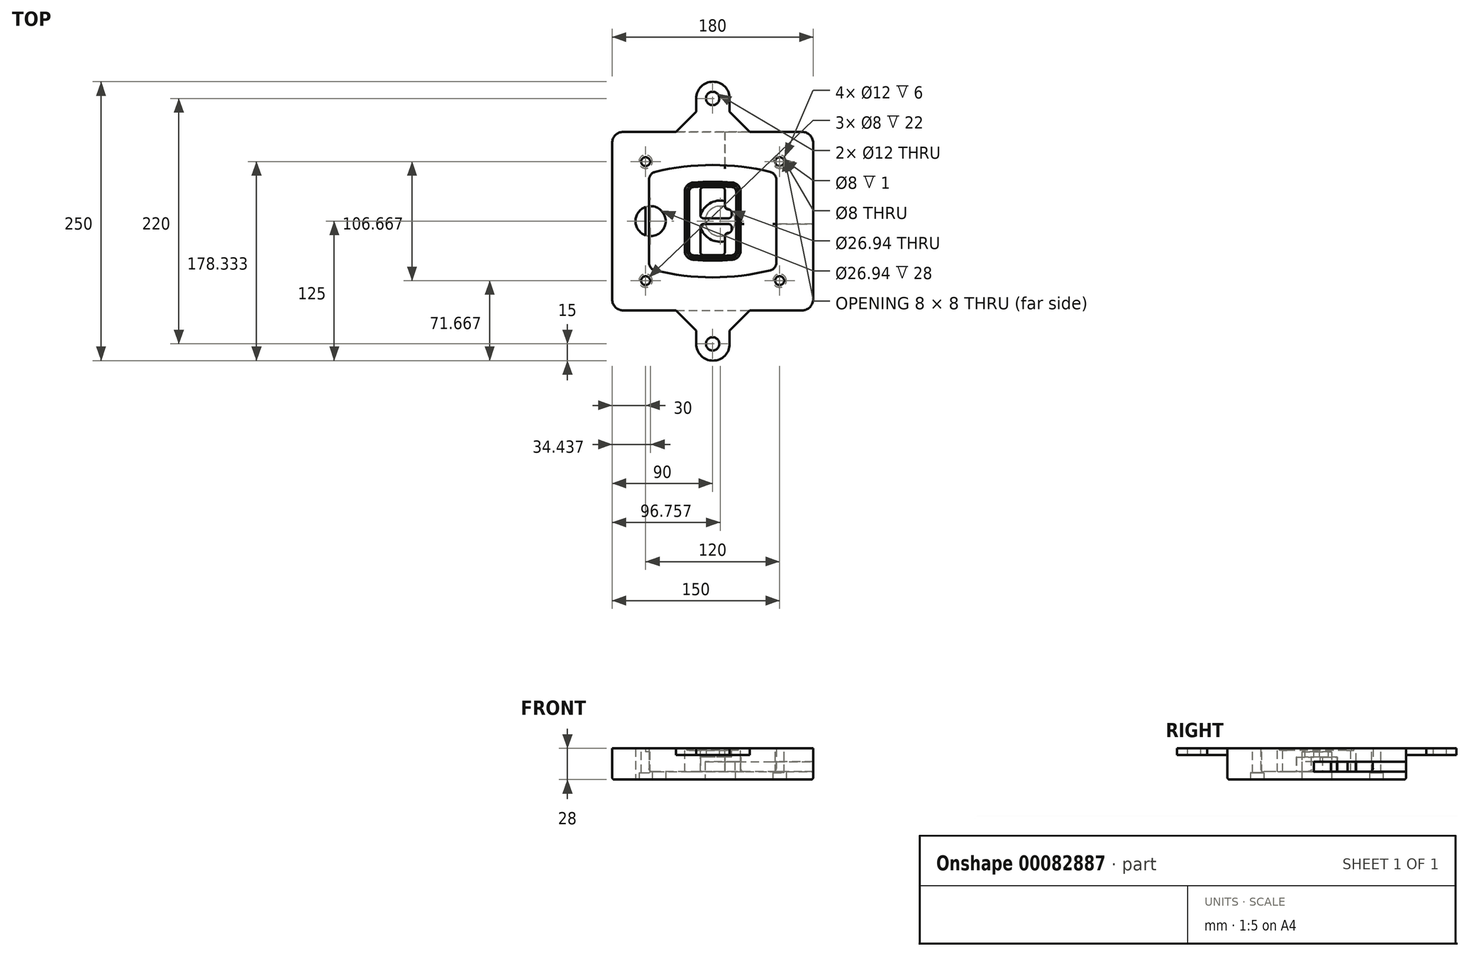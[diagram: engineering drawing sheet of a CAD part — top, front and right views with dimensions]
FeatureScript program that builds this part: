
annotation { "Feature Type Name" : "Feature", "Feature Type Description" : "" }
export const myFeature = defineFeature(function(context is Context, id is Id, definition is map)
    precondition{}
    {
        {
            var Q0;
            Q0=qCreatedBy(makeId("Top.planeOp"),FACE);
            var sketch = newSketch(context, id + "F0", { "sketchPlane" : qUnion([Q0])});
            skPoint(sketch, "E0.rect.middle", {"position": v(0, 0) * mm});
            skLineSegment(sketch, "E1.bottom", {"start": v(-80, -80) * mm, "end": v(80, -80) * mm});
            skLineSegment(sketch, "E1.top", {"start": v(-80, 80) * mm, "end": v(80, 80) * mm});
            skLineSegment(sketch, "E1.left", {"start": v(-90, -70) * mm, "end": v(-90, 70) * mm});
            skLineSegment(sketch, "E1.right", {"start": v(90, -70) * mm, "end": v(90, 70) * mm});
            skLineSegment(sketch, "E2", {"start": v(-90, 80) * mm, "end": v(90, -80) * mm, "construction": true});
            skLineSegment(sketch, "E3", {"start": v(90, 80) * mm, "end": v(-90, -80) * mm, "construction": true});
            skCircle(sketch, "E4", {"center": v(-60, 53.33) * mm, "radius": 4 * mm});
            skCircle(sketch, "E5", {"center": v(60, 53.33) * mm, "radius": 4 * mm});
            skCircle(sketch, "E6", {"center": v(60, -53.33) * mm, "radius": 4 * mm});
            skCircle(sketch, "E7", {"center": v(-60, -53.33) * mm, "radius": 4 * mm});
            skLineSegment(sketch, "E8", {"start": v(-60, 53.33) * mm, "end": v(60, 53.33) * mm, "construction": true});
            skLineSegment(sketch, "E9", {"start": v(60, 53.33) * mm, "end": v(60, -53.33) * mm, "construction": true});
            skLineSegment(sketch, "E10", {"start": v(60, -53.33) * mm, "end": v(-60, -53.33) * mm, "construction": true});
            skLineSegment(sketch, "E11", {"start": v(-60, -53.33) * mm, "end": v(-60, 53.33) * mm, "construction": true});
            skLineSegment(sketch, "E12", {"start": v(-60, 37.3) * mm, "end": v(-60, -37.3) * mm});
            skLineSegment(sketch, "E13", {"start": v(60, 37.3) * mm, "end": v(60, -37.3) * mm});
            skArc(sketch, "E14", {"start": v(52.38, 47.01) * mm, "mid": v(0, 53.33) * mm, "end": v(-52.38, 47.01) * mm});
            skArc(sketch, "E15", {"start": v(-52.38, -47.01) * mm, "mid": v(0, -53.33) * mm, "end": v(52.38, -47.01) * mm});
            skLineSegment(sketch, "E16", {"start": v(-60, 0) * mm, "end": v(60, 0) * mm, "construction": true});
            skPoint(sketch, "E17.visualSharp", {"position": v(-60, -45) * mm});
            skArc(sketch, "E17.filletArc", {"start": v(-60, -37.3) * mm, "mid": v(-57.87, -43.47) * mm, "end": v(-52.38, -47.01) * mm});
            skPoint(sketch, "E18.visualSharp", {"position": v(-60, 45) * mm});
            skArc(sketch, "E18.filletArc", {"start": v(-52.38, 47.01) * mm, "mid": v(-57.87, 43.47) * mm, "end": v(-60, 37.3) * mm});
            skPoint(sketch, "E19.visualSharp", {"position": v(60, 45) * mm});
            skArc(sketch, "E19.filletArc", {"start": v(60, 37.3) * mm, "mid": v(57.87, 43.47) * mm, "end": v(52.38, 47.01) * mm});
            skPoint(sketch, "E20.visualSharp", {"position": v(60, -45) * mm});
            skArc(sketch, "E20.filletArc", {"start": v(52.38, -47.01) * mm, "mid": v(57.87, -43.47) * mm, "end": v(60, -37.3) * mm});
            skPoint(sketch, "E21.visualSharp", {"position": v(-90, 80) * mm});
            skArc(sketch, "E21.filletArc", {"start": v(-80, 80) * mm, "mid": v(-87.07, 77.07) * mm, "end": v(-90, 70) * mm});
            skPoint(sketch, "E22.visualSharp", {"position": v(90, 80) * mm});
            skArc(sketch, "E22.filletArc", {"start": v(90, 70) * mm, "mid": v(87.07, 77.07) * mm, "end": v(80, 80) * mm});
            skPoint(sketch, "E23.visualSharp", {"position": v(90, -80) * mm});
            skArc(sketch, "E23.filletArc", {"start": v(80, -80) * mm, "mid": v(87.07, -77.07) * mm, "end": v(90, -70) * mm});
            skPoint(sketch, "E24.visualSharp", {"position": v(-90, -80) * mm});
            skArc(sketch, "E24.filletArc", {"start": v(-90, -70) * mm, "mid": v(-87.07, -77.07) * mm, "end": v(-80, -80) * mm});
            skArc(sketch, "E25.0", {"start": v(57, 37.3) * mm, "mid": v(55.5, 41.62) * mm, "end": v(51.67, 44.1) * mm});
            skLineSegment(sketch, "E25.1", {"start": v(57, 37.3) * mm, "end": v(57, -37.3) * mm});
            skArc(sketch, "E25.2", {"start": v(51.67, -44.1) * mm, "mid": v(55.5, -41.62) * mm, "end": v(57, -37.3) * mm});
            skArc(sketch, "E25.3", {"start": v(-51.67, -44.1) * mm, "mid": v(0, -50.33) * mm, "end": v(51.67, -44.1) * mm});
            skArc(sketch, "E25.4", {"start": v(-57, -37.3) * mm, "mid": v(-55.5, -41.62) * mm, "end": v(-51.67, -44.1) * mm});
            skArc(sketch, "E25.5", {"start": v(51.67, 44.1) * mm, "mid": v(0, 50.33) * mm, "end": v(-51.67, 44.1) * mm});
            skLineSegment(sketch, "E25.6", {"start": v(-57, 37.3) * mm, "end": v(-57, -37.3) * mm});
            skArc(sketch, "E25.7", {"start": v(-51.67, 44.1) * mm, "mid": v(-55.5, 41.62) * mm, "end": v(-57, 37.3) * mm});
            skArc(sketch, "E26.0", {"start": v(-53.33, 50.9) * mm, "mid": v(-61.01, 45.94) * mm, "end": v(-64, 37.3) * mm});
            skArc(sketch, "E26.1", {"start": v(53.33, 50.9) * mm, "mid": v(0, 57.33) * mm, "end": v(-53.33, 50.9) * mm});
            skArc(sketch, "E26.2", {"start": v(64, 37.3) * mm, "mid": v(61.01, 45.94) * mm, "end": v(53.33, 50.9) * mm});
            skLineSegment(sketch, "E26.3", {"start": v(64, 37.3) * mm, "end": v(64, -37.3) * mm});
            skArc(sketch, "E26.4", {"start": v(53.33, -50.9) * mm, "mid": v(61.01, -45.94) * mm, "end": v(64, -37.3) * mm});
            skLineSegment(sketch, "E26.5", {"start": v(-64, 37.3) * mm, "end": v(-64, -37.3) * mm});
            skArc(sketch, "E26.6", {"start": v(-53.33, -50.9) * mm, "mid": v(0, -57.33) * mm, "end": v(53.33, -50.9) * mm});
            skArc(sketch, "E26.7", {"start": v(-64, -37.3) * mm, "mid": v(-61.01, -45.94) * mm, "end": v(-53.33, -50.9) * mm});
            skSolve(sketch);
        }
        {
            var Q0;
            Q0=makeQuery(id+"F0.imprint","IMPRINT",FACE,{"disambiguationData":[TD([[makeQuery(id+"F0.imprint","IMPRINT",EDGE,{"derivedFrom":sQuery(id+"F0.wireOp",EDGE,"E1.bottom")}),1.0]])]});
            var Q1;
            Q1=makeQuery(id+"F0.imprint","IMPRINT",FACE,{"disambiguationData":[TD([[makeQuery(id+"F0.imprint","IMPRINT",EDGE,{"derivedFrom":sQuery(id+"F0.wireOp",EDGE,"E12")}),1.0]])]});
            var Q2;
            Q2=makeQuery(id+"F0.imprint","IMPRINT",FACE,{"disambiguationData":[TD([[makeQuery(id+"F0.imprint","IMPRINT",EDGE,{"derivedFrom":sQuery(id+"F0.wireOp",EDGE,"E25.0")}),1.0]])]});
            var Q3;
            Q3=makeQuery(id+"F0.imprint","IMPRINT",FACE,{"disambiguationData":[TD([[makeQuery(id+"F0.imprint","IMPRINT",EDGE,{"derivedFrom":sQuery(id+"F0.wireOp",EDGE,"E12")}),-1.0]])]});
            extrude(context, id + "F1", {"entities" : qUnion([Q0, Q1, Q2, Q3]), "oppositeDirection" : true, "depth" : 25 * mm});
        }
        {
            var Q0;
            Q0=makeQuery(id+"F0.imprint","IMPRINT",FACE,{"disambiguationData":[TD([[makeQuery(id+"F0.imprint","IMPRINT",EDGE,{"derivedFrom":sQuery(id+"F0.wireOp",EDGE,"E12")}),1.0]])]});
            extrude(context, id + "F2", {"entities" : qUnion([Q0]), "operationType" : NewBodyOperationType.ADD, "depth" : 3 * mm});
        }
        {
            var Q0;
            Q0=makeQuery(id+"F0.imprint","IMPRINT",FACE,{"disambiguationData":[TD([[makeQuery(id+"F0.imprint","IMPRINT",EDGE,{"derivedFrom":sQuery(id+"F0.wireOp",EDGE,"E25.0")}),1.0]])]});
            extrude(context, id + "F3", {"entities" : qUnion([Q0]), "operationType" : NewBodyOperationType.REMOVE, "oppositeDirection" : true, "depth" : 18 * mm});
        }
        {
            var Q0;
            Q0=makeQuery(id+"F2.opExtrude","CAP_FACE",FACE,{"disambiguationData":[OSD([sQuery(id+"F0.wireOp",EDGE,"E12"),sQuery(id+"F0.wireOp",EDGE,"E13"),sQuery(id+"F0.wireOp",EDGE,"E14"),sQuery(id+"F0.wireOp",EDGE,"E15"),sQuery(id+"F0.wireOp",EDGE,"E17.filletArc"),sQuery(id+"F0.wireOp",EDGE,"E18.filletArc"),sQuery(id+"F0.wireOp",EDGE,"E19.filletArc"),sQuery(id+"F0.wireOp",EDGE,"E20.filletArc"),sQuery(id+"F0.wireOp",EDGE,"E25.0"),sQuery(id+"F0.wireOp",EDGE,"E25.1"),sQuery(id+"F0.wireOp",EDGE,"E25.2"),sQuery(id+"F0.wireOp",EDGE,"E25.3"),sQuery(id+"F0.wireOp",EDGE,"E25.4"),sQuery(id+"F0.wireOp",EDGE,"E25.5"),sQuery(id+"F0.wireOp",EDGE,"E25.6"),sQuery(id+"F0.wireOp",EDGE,"E25.7")])],"isStart":false});
            var sketch = newSketch(context, id + "F4", { "sketchPlane" : qUnion([Q0])});
            skArc(sketch, "E27.0", {"start": v(-17.7, -34.56) * mm, "mid": v(0, -35.33) * mm, "end": v(17.7, -34.56) * mm});
            skArc(sketch, "E28.0", {"start": v(17.7, 34.56) * mm, "mid": v(0, 35.33) * mm, "end": v(-17.7, 34.56) * mm});
            skLineSegment(sketch, "E29", {"start": v(-25, 26.59) * mm, "end": v(-25, -26.59) * mm});
            skLineSegment(sketch, "E30", {"start": v(25, 26.59) * mm, "end": v(25, -26.59) * mm});
            skLineSegment(sketch, "E31", {"start": v(-25, 33.78) * mm, "end": v(25, 33.78) * mm, "construction": true});
            skLineSegment(sketch, "E32", {"start": v(-25, -33.78) * mm, "end": v(25, -33.78) * mm, "construction": true});
            skPoint(sketch, "E33.visualSharp", {"position": v(-25, 33.78) * mm});
            skArc(sketch, "E33.filletArc", {"start": v(-17.7, 34.56) * mm, "mid": v(-22.9, 32) * mm, "end": v(-25, 26.59) * mm});
            skPoint(sketch, "E34.visualSharp", {"position": v(25, 33.78) * mm});
            skArc(sketch, "E34.filletArc", {"start": v(25, 26.59) * mm, "mid": v(22.9, 32) * mm, "end": v(17.7, 34.56) * mm});
            skPoint(sketch, "E35.visualSharp", {"position": v(25, -33.78) * mm});
            skArc(sketch, "E35.filletArc", {"start": v(17.7, -34.56) * mm, "mid": v(22.9, -32) * mm, "end": v(25, -26.59) * mm});
            skPoint(sketch, "E36.visualSharp", {"position": v(-25, -33.78) * mm});
            skArc(sketch, "E36.filletArc", {"start": v(-25, -26.59) * mm, "mid": v(-22.9, -32) * mm, "end": v(-17.7, -34.56) * mm});
            skArc(sketch, "E37.0", {"start": v(51.67, 44.1) * mm, "mid": v(0, 50.33) * mm, "end": v(-51.67, 44.1) * mm});
            skArc(sketch, "E37.1", {"start": v(-51.67, 44.1) * mm, "mid": v(-55.5, 41.62) * mm, "end": v(-57, 37.3) * mm});
            skLineSegment(sketch, "E37.2", {"start": v(-57, 37.3) * mm, "end": v(-57, -37.3) * mm});
            skArc(sketch, "E37.3", {"start": v(-57, -37.3) * mm, "mid": v(-55.5, -41.62) * mm, "end": v(-51.67, -44.1) * mm});
            skArc(sketch, "E37.4", {"start": v(-51.67, -44.1) * mm, "mid": v(0, -50.33) * mm, "end": v(51.67, -44.1) * mm});
            skArc(sketch, "E37.5", {"start": v(51.67, -44.1) * mm, "mid": v(55.5, -41.62) * mm, "end": v(57, -37.3) * mm});
            skLineSegment(sketch, "E37.6", {"start": v(57, 37.3) * mm, "end": v(57, -37.3) * mm});
            skArc(sketch, "E37.7", {"start": v(57, 37.3) * mm, "mid": v(55.5, 41.62) * mm, "end": v(51.67, 44.1) * mm});
            skLineSegment(sketch, "E38.0", {"start": v(23, 26.59) * mm, "end": v(23, -26.59) * mm});
            skArc(sketch, "E38.1", {"start": v(17.53, -32.56) * mm, "mid": v(21.42, -30.64) * mm, "end": v(23, -26.59) * mm});
            skArc(sketch, "E38.2", {"start": v(-17.53, -32.56) * mm, "mid": v(0, -33.33) * mm, "end": v(17.53, -32.56) * mm});
            skArc(sketch, "E38.3", {"start": v(-23, -26.59) * mm, "mid": v(-21.42, -30.64) * mm, "end": v(-17.53, -32.56) * mm});
            skLineSegment(sketch, "E38.4", {"start": v(-23, 26.59) * mm, "end": v(-23, -26.59) * mm});
            skArc(sketch, "E38.5", {"start": v(23, 26.59) * mm, "mid": v(21.42, 30.64) * mm, "end": v(17.53, 32.56) * mm});
            skArc(sketch, "E38.6", {"start": v(-17.53, 32.56) * mm, "mid": v(-21.42, 30.64) * mm, "end": v(-23, 26.59) * mm});
            skArc(sketch, "E38.7", {"start": v(17.53, 32.56) * mm, "mid": v(0, 33.33) * mm, "end": v(-17.53, 32.56) * mm});
            skArc(sketch, "E39.0", {"start": v(21, 26.59) * mm, "mid": v(19.95, 29.29) * mm, "end": v(17.35, 30.57) * mm});
            skLineSegment(sketch, "E39.1", {"start": v(21, 26.59) * mm, "end": v(21, -26.59) * mm});
            skArc(sketch, "E39.2", {"start": v(17.35, -30.57) * mm, "mid": v(19.95, -29.29) * mm, "end": v(21, -26.59) * mm});
            skArc(sketch, "E39.3", {"start": v(-17.35, -30.57) * mm, "mid": v(0, -31.33) * mm, "end": v(17.35, -30.57) * mm});
            skArc(sketch, "E39.4", {"start": v(-21, -26.59) * mm, "mid": v(-19.95, -29.29) * mm, "end": v(-17.35, -30.57) * mm});
            skArc(sketch, "E39.5", {"start": v(17.35, 30.57) * mm, "mid": v(0, 31.33) * mm, "end": v(-17.35, 30.57) * mm});
            skLineSegment(sketch, "E39.6", {"start": v(-21, 26.59) * mm, "end": v(-21, -26.59) * mm});
            skArc(sketch, "E39.7", {"start": v(-17.35, 30.57) * mm, "mid": v(-19.95, 29.29) * mm, "end": v(-21, 26.59) * mm});
            skLineSegment(sketch, "E40", {"start": v(-25, 0) * mm, "end": v(25, 0) * mm, "construction": true});
            skLineSegment(sketch, "E41", {"start": v(-11, 5.5) * mm, "end": v(-11, 27.5) * mm});
            skLineSegment(sketch, "E42", {"start": v(-8, 30.5) * mm, "end": v(8, 30.5) * mm});
            skLineSegment(sketch, "E43", {"start": v(11, 27.5) * mm, "end": v(11, 13.5) * mm});
            skLineSegment(sketch, "E44", {"start": v(14, 10.5) * mm, "end": v(14, 10.5) * mm});
            skLineSegment(sketch, "E45", {"start": v(17, 7.5) * mm, "end": v(17, 5.5) * mm});
            skLineSegment(sketch, "E46", {"start": v(14, 2.5) * mm, "end": v(-8, 2.5) * mm});
            skPoint(sketch, "E47.visualSharp", {"position": v(-11, 30.5) * mm});
            skArc(sketch, "E47.filletArc", {"start": v(-8, 30.5) * mm, "mid": v(-10.12, 29.62) * mm, "end": v(-11, 27.5) * mm});
            skPoint(sketch, "E48.visualSharp", {"position": v(11, 30.5) * mm});
            skArc(sketch, "E48.filletArc", {"start": v(11, 27.5) * mm, "mid": v(10.12, 29.62) * mm, "end": v(8, 30.5) * mm});
            skPoint(sketch, "E49.visualSharp", {"position": v(11, 10.5) * mm});
            skArc(sketch, "E49.filletArc", {"start": v(11, 13.5) * mm, "mid": v(11.88, 11.38) * mm, "end": v(14, 10.5) * mm});
            skPoint(sketch, "E50.visualSharp", {"position": v(17, 10.5) * mm});
            skArc(sketch, "E50.filletArc", {"start": v(17, 7.5) * mm, "mid": v(16.12, 9.62) * mm, "end": v(14, 10.5) * mm});
            skPoint(sketch, "E51.visualSharp", {"position": v(17, 2.5) * mm});
            skArc(sketch, "E51.filletArc", {"start": v(14, 2.5) * mm, "mid": v(16.12, 3.38) * mm, "end": v(17, 5.5) * mm});
            skPoint(sketch, "E52.visualSharp", {"position": v(-11, 2.5) * mm});
            skArc(sketch, "E52.filletArc", {"start": v(-11, 5.5) * mm, "mid": v(-10.12, 3.38) * mm, "end": v(-8, 2.5) * mm});
            skLineSegment(sketch, "E53.0.MirrorCS", {"start": v(14, -2.5) * mm, "end": v(-8, -2.5) * mm});
            skArc(sketch, "E54.0.MirrorCS", {"start": v(-11, -5.5) * mm, "mid": v(-10.12, -3.38) * mm, "end": v(-8, -2.5) * mm});
            skLineSegment(sketch, "E55.0.MirrorCS", {"start": v(-11, -5.5) * mm, "end": v(-11, -27.5) * mm});
            skArc(sketch, "E56.0.MirrorCS", {"start": v(-8, -30.5) * mm, "mid": v(-10.12, -29.62) * mm, "end": v(-11, -27.5) * mm});
            skLineSegment(sketch, "E57.0.MirrorCS", {"start": v(-8, -30.5) * mm, "end": v(8, -30.5) * mm});
            skArc(sketch, "E58.0.MirrorCS", {"start": v(11, -27.5) * mm, "mid": v(10.12, -29.62) * mm, "end": v(8, -30.5) * mm});
            skLineSegment(sketch, "E59.0.MirrorCS", {"start": v(11, -27.5) * mm, "end": v(11, -13.5) * mm});
            skArc(sketch, "E60.0.MirrorCS", {"start": v(11, -13.5) * mm, "mid": v(11.88, -11.38) * mm, "end": v(14, -10.5) * mm});
            skArc(sketch, "E61.0.MirrorCS", {"start": v(17, -7.5) * mm, "mid": v(16.12, -9.62) * mm, "end": v(14, -10.5) * mm});
            skLineSegment(sketch, "E62.0.MirrorCS", {"start": v(17, -7.5) * mm, "end": v(17, -5.5) * mm});
            skArc(sketch, "E63.0.MirrorCS", {"start": v(14, -2.5) * mm, "mid": v(16.12, -3.38) * mm, "end": v(17, -5.5) * mm});
            skSolve(sketch);
        }
        {
            var Q0;
            Q0=makeQuery(id+"F4.imprint","IMPRINT",FACE,{"disambiguationData":[TD([[makeQuery(id+"F4.imprint","IMPRINT",EDGE,{"derivedFrom":sQuery(id+"F4.wireOp",EDGE,"E27.0")}),1.0]])]});
            var Q1;
            Q1=makeQuery(id+"F4.imprint","IMPRINT",FACE,{"disambiguationData":[TD([[makeQuery(id+"F4.imprint","IMPRINT",EDGE,{"derivedFrom":sQuery(id+"F4.wireOp",EDGE,"E38.0")}),-1.0]])]});
            var Q2;
            Q2=makeQuery(id+"F4.imprint","IMPRINT",FACE,{"disambiguationData":[TD([[makeQuery(id+"F4.imprint","IMPRINT",EDGE,{"derivedFrom":sQuery(id+"F4.wireOp",EDGE,"E39.0")}),1.0]])]});
            extrude(context, id + "F5", {"entities" : qUnion([Q0, Q1, Q2]), "operationType" : NewBodyOperationType.ADD, "endBound" : BoundingType.UP_TO_NEXT, "oppositeDirection" : true, "depth" : 25 * mm});
        }
        {
            var Q0;
            Q0=makeQuery(id+"F4.imprint","IMPRINT",FACE,{"disambiguationData":[TD([[makeQuery(id+"F4.imprint","IMPRINT",EDGE,{"derivedFrom":sQuery(id+"F4.wireOp",EDGE,"E38.0")}),-1.0]])]});
            extrude(context, id + "F6", {"entities" : qUnion([Q0]), "operationType" : NewBodyOperationType.REMOVE, "oppositeDirection" : true, "depth" : 2 * mm});
        }
        {
            var Q0;
            Q0=makeQuery(id+"F1.opExtrude","CAP_FACE",FACE,{"disambiguationData":[OSD([sQuery(id+"F0.wireOp",EDGE,"E1.bottom"),sQuery(id+"F0.wireOp",EDGE,"E1.top"),sQuery(id+"F0.wireOp",EDGE,"E1.left"),sQuery(id+"F0.wireOp",EDGE,"E1.right"),sQuery(id+"F0.wireOp",EDGE,"E4"),sQuery(id+"F0.wireOp",EDGE,"E5"),sQuery(id+"F0.wireOp",EDGE,"E6"),sQuery(id+"F0.wireOp",EDGE,"E7"),sQuery(id+"F0.wireOp",EDGE,"E21.filletArc"),sQuery(id+"F0.wireOp",EDGE,"E22.filletArc"),sQuery(id+"F0.wireOp",EDGE,"E23.filletArc"),sQuery(id+"F0.wireOp",EDGE,"E24.filletArc")])],"isStart":false});
            var sketch = newSketch(context, id + "F7", { "sketchPlane" : qUnion([Q0])});
            skCircle(sketch, "E64", {"center": v(6.76, 0) * mm, "radius": 13.47 * mm});
            skCircle(sketch, "E65", {"center": v(-55.56, 0) * mm, "radius": 13.47 * mm});
            skLineSegment(sketch, "E66", {"start": v(90, 0) * mm, "end": v(-90, 0) * mm});
            skCircle(sketch, "E67", {"center": v(6.76, 0) * mm, "radius": 18.47 * mm});
            skCircle(sketch, "E68", {"center": v(60, -53.33) * mm, "radius": 6 * mm});
            skCircle(sketch, "E69", {"center": v(-60, -53.33) * mm, "radius": 6 * mm});
            skCircle(sketch, "E70", {"center": v(-60, 53.33) * mm, "radius": 6 * mm});
            skCircle(sketch, "E71", {"center": v(60, 53.33) * mm, "radius": 6 * mm});
            skSolve(sketch);
        }
        {
            var Q0;
            {var subQ1=sQuery(id+"F7.wireOp",EDGE,"E66");var subQ4=sQuery(id+"F7.wireOp",EDGE,"E64");var subQ6=makeQuery(id+"F7.imprint","INTERSECT",VERTEX,{"disambiguationData":[OD(0.0)],"derivedFrom":[subQ4,subQ1]});Q0=makeQuery(id+"F7.imprint","IMPRINT",FACE,{"disambiguationData":[TD([[makeQuery(id+"F7.imprint","IMPRINT",EDGE,{"disambiguationData":[TD([[subQ6,-1.0]])],"derivedFrom":subQ4}),-1.0]])]});}
            var Q1;
            {var subQ0=sQuery(id+"F7.wireOp",EDGE,"E66");var subQ1=sQuery(id+"F7.wireOp",EDGE,"E64");var subQ3=makeQuery(id+"F7.imprint","INTERSECT",VERTEX,{"disambiguationData":[OD(0.0)],"derivedFrom":[subQ1,subQ0]});Q1=makeQuery(id+"F7.imprint","IMPRINT",FACE,{"disambiguationData":[TD([[makeQuery(id+"F7.imprint","IMPRINT",EDGE,{"disambiguationData":[TD([[subQ3,-1.0]])],"derivedFrom":subQ1}),1.0]])]});}
            var Q2;
            {var subQ0=sQuery(id+"F7.wireOp",EDGE,"E66");var subQ1=sQuery(id+"F7.wireOp",EDGE,"E64");var subQ3=makeQuery(id+"F7.imprint","INTERSECT",VERTEX,{"disambiguationData":[OD(0.0)],"derivedFrom":[subQ1,subQ0]});Q2=makeQuery(id+"F7.imprint","IMPRINT",FACE,{"disambiguationData":[TD([[makeQuery(id+"F7.imprint","IMPRINT",EDGE,{"disambiguationData":[TD([[subQ3,1.0]])],"derivedFrom":subQ1}),1.0]])]});}
            var Q3;
            {var subQ1=sQuery(id+"F7.wireOp",EDGE,"E66");var subQ4=sQuery(id+"F7.wireOp",EDGE,"E64");var subQ6=makeQuery(id+"F7.imprint","INTERSECT",VERTEX,{"disambiguationData":[OD(0.0)],"derivedFrom":[subQ4,subQ1]});Q3=makeQuery(id+"F7.imprint","IMPRINT",FACE,{"disambiguationData":[TD([[makeQuery(id+"F7.imprint","IMPRINT",EDGE,{"disambiguationData":[TD([[subQ6,1.0]])],"derivedFrom":subQ4}),-1.0]])]});}
            extrude(context, id + "F8", {"entities" : qUnion([Q0, Q1, Q2, Q3]), "operationType" : NewBodyOperationType.ADD, "oppositeDirection" : true, "depth" : 20 * mm});
        }
        {
            var Q0;
            {var subQ0=sQuery(id+"F7.wireOp",EDGE,"E66");var subQ1=sQuery(id+"F7.wireOp",EDGE,"E64");var subQ3=makeQuery(id+"F7.imprint","INTERSECT",VERTEX,{"disambiguationData":[OD(0.0)],"derivedFrom":[subQ1,subQ0]});Q0=makeQuery(id+"F7.imprint","IMPRINT",FACE,{"disambiguationData":[TD([[makeQuery(id+"F7.imprint","IMPRINT",EDGE,{"disambiguationData":[TD([[subQ3,-1.0]])],"derivedFrom":subQ1}),1.0]])]});}
            var Q1;
            {var subQ0=sQuery(id+"F7.wireOp",EDGE,"E66");var subQ1=sQuery(id+"F7.wireOp",EDGE,"E64");var subQ3=makeQuery(id+"F7.imprint","INTERSECT",VERTEX,{"disambiguationData":[OD(0.0)],"derivedFrom":[subQ1,subQ0]});Q1=makeQuery(id+"F7.imprint","IMPRINT",FACE,{"disambiguationData":[TD([[makeQuery(id+"F7.imprint","IMPRINT",EDGE,{"disambiguationData":[TD([[subQ3,1.0]])],"derivedFrom":subQ1}),1.0]])]});}
            extrude(context, id + "F9", {"entities" : qUnion([Q0, Q1]), "operationType" : NewBodyOperationType.REMOVE, "oppositeDirection" : true, "depth" : 16 * mm});
        }
        {
            var Q0;
            {var subQ0=sQuery(id+"F7.wireOp",EDGE,"E66");var subQ1=sQuery(id+"F7.wireOp",EDGE,"E65");var subQ3=makeQuery(id+"F7.imprint","INTERSECT",VERTEX,{"disambiguationData":[OD(0.0)],"derivedFrom":[subQ1,subQ0]});Q0=makeQuery(id+"F7.imprint","IMPRINT",FACE,{"disambiguationData":[TD([[makeQuery(id+"F7.imprint","IMPRINT",EDGE,{"disambiguationData":[TD([[subQ3,-1.0]])],"derivedFrom":subQ1}),1.0]])]});}
            var Q1;
            {var subQ0=sQuery(id+"F7.wireOp",EDGE,"E66");var subQ1=sQuery(id+"F7.wireOp",EDGE,"E65");var subQ3=makeQuery(id+"F7.imprint","INTERSECT",VERTEX,{"disambiguationData":[OD(0.0)],"derivedFrom":[subQ1,subQ0]});Q1=makeQuery(id+"F7.imprint","IMPRINT",FACE,{"disambiguationData":[TD([[makeQuery(id+"F7.imprint","IMPRINT",EDGE,{"disambiguationData":[TD([[subQ3,1.0]])],"derivedFrom":subQ1}),1.0]])]});}
            extrude(context, id + "F10", {"entities" : qUnion([Q0, Q1]), "operationType" : NewBodyOperationType.REMOVE, "oppositeDirection" : true, "depth" : 25 * mm});
        }
        {
            var Q0;
            Q0=makeQuery(id+"F7.imprint","IMPRINT",FACE,{"disambiguationData":[TD([[makeQuery(id+"F7.imprint","IMPRINT",EDGE,{"derivedFrom":sQuery(id+"F7.wireOp",EDGE,"E68")}),1.0]])]});
            var Q1;
            Q1=makeQuery(id+"F7.imprint","IMPRINT",FACE,{"disambiguationData":[TD([[makeQuery(id+"F7.imprint","IMPRINT",EDGE,{"derivedFrom":makeQuery(id+"F1.opExtrude","CAP_EDGE",EDGE,{"disambiguationData":[OSD([sQuery(id+"F0.wireOp",EDGE,"E5")])],"isStart":false})}),-1.0]])]});
            var Q2;
            Q2=makeQuery(id+"F7.imprint","IMPRINT",FACE,{"disambiguationData":[TD([[makeQuery(id+"F7.imprint","IMPRINT",EDGE,{"derivedFrom":sQuery(id+"F7.wireOp",EDGE,"E69")}),1.0]])]});
            var Q3;
            Q3=makeQuery(id+"F7.imprint","IMPRINT",FACE,{"disambiguationData":[TD([[makeQuery(id+"F7.imprint","IMPRINT",EDGE,{"derivedFrom":makeQuery(id+"F1.opExtrude","CAP_EDGE",EDGE,{"disambiguationData":[OSD([sQuery(id+"F0.wireOp",EDGE,"E4")])],"isStart":false})}),-1.0]])]});
            var Q4;
            Q4=makeQuery(id+"F7.imprint","IMPRINT",FACE,{"disambiguationData":[TD([[makeQuery(id+"F7.imprint","IMPRINT",EDGE,{"derivedFrom":sQuery(id+"F7.wireOp",EDGE,"E70")}),1.0]])]});
            var Q5;
            Q5=makeQuery(id+"F7.imprint","IMPRINT",FACE,{"disambiguationData":[TD([[makeQuery(id+"F7.imprint","IMPRINT",EDGE,{"derivedFrom":makeQuery(id+"F1.opExtrude","CAP_EDGE",EDGE,{"disambiguationData":[OSD([sQuery(id+"F0.wireOp",EDGE,"E7")])],"isStart":false})}),-1.0]])]});
            var Q6;
            Q6=makeQuery(id+"F7.imprint","IMPRINT",FACE,{"disambiguationData":[TD([[makeQuery(id+"F7.imprint","IMPRINT",EDGE,{"derivedFrom":sQuery(id+"F7.wireOp",EDGE,"E71")}),1.0]])]});
            var Q7;
            Q7=makeQuery(id+"F7.imprint","IMPRINT",FACE,{"disambiguationData":[TD([[makeQuery(id+"F7.imprint","IMPRINT",EDGE,{"derivedFrom":makeQuery(id+"F1.opExtrude","CAP_EDGE",EDGE,{"disambiguationData":[OSD([sQuery(id+"F0.wireOp",EDGE,"E6")])],"isStart":false})}),-1.0]])]});
            extrude(context, id + "F11", {"entities" : qUnion([Q0, Q1, Q2, Q3, Q4, Q5, Q6, Q7]), "operationType" : NewBodyOperationType.REMOVE, "oppositeDirection" : true, "depth" : 6 * mm});
        }
        {
            var Q0;
            Q0=makeQuery(id+"F9.boolean.opBoolean","COPY",FACE,{"derivedFrom":makeQuery(id+"F9.opExtrude","CAP_FACE",FACE,{"disambiguationData":[OSD([sQuery(id+"F7.wireOp",EDGE,"E64")])],"isStart":false})});
            var sketch = newSketch(context, id + "F12", { "sketchPlane" : qUnion([Q0])});
            skArc(sketch, "E72.0", {"start": v(11, -88.19) * mm, "mid": v(97.1, -83.6) * mm, "end": v(92.5, 2.5) * mm});
            skLineSegment(sketch, "E72.1", {"start": v(11, -17.97) * mm, "end": v(11, -17.97) * mm});
            skLineSegment(sketch, "E73", {"start": v(92.5, -105.13) * mm, "end": v(102.3, -105.13) * mm});
            skLineSegment(sketch, "E74.0", {"start": v(92.5, 2.5) * mm, "end": v(14, 2.5) * mm});
            skArc(sketch, "E74.1", {"start": v(14, 2.5) * mm, "mid": v(16.12, 3.38) * mm, "end": v(17, 5.5) * mm});
            skLineSegment(sketch, "E74.2", {"start": v(17, 7.5) * mm, "end": v(17, 5.5) * mm});
            skArc(sketch, "E74.3", {"start": v(17, 7.5) * mm, "mid": v(16.12, 9.62) * mm, "end": v(14, 10.5) * mm});
            skArc(sketch, "E74.4", {"start": v(11, 13.5) * mm, "mid": v(11.88, 11.38) * mm, "end": v(14, 10.5) * mm});
            skLineSegment(sketch, "E74.5", {"start": v(11, 13.5) * mm, "end": v(11, -88.19) * mm});
            skLineSegment(sketch, "E74.7", {"start": v(92.5, -2.5) * mm, "end": v(14, -2.5) * mm});
            skArc(sketch, "E74.8", {"start": v(14, -2.5) * mm, "mid": v(16.12, -3.38) * mm, "end": v(17, -5.5) * mm});
            skLineSegment(sketch, "E74.9", {"start": v(17, -7.5) * mm, "end": v(17, -5.5) * mm});
            skArc(sketch, "E74.10", {"start": v(17, -7.5) * mm, "mid": v(16.12, -9.62) * mm, "end": v(14, -10.5) * mm});
            skArc(sketch, "E74.11", {"start": v(11, -13.5) * mm, "mid": v(11.88, -11.38) * mm, "end": v(14, -10.5) * mm});
            skLineSegment(sketch, "E74.12", {"start": v(11, -17.97) * mm, "end": v(11, -13.5) * mm});
            skPoint(sketch, "E75.orphan", {"position": v(11, -27.5) * mm});
            skPoint(sketch, "E76.orphan", {"position": v(-8, -2.5) * mm});
            skPoint(sketch, "E77.orphan", {"position": v(-8, 2.5) * mm});
            skPoint(sketch, "E78.orphan", {"position": v(11, 27.5) * mm});
            skSolve(sketch);
        }
        {
            var Q0;
            {var subQ7=sQuery(id+"F12.wireOp",EDGE,"E72.0");var subQ14=sQuery(id+"F12.wireOp",EDGE,"E72.1");var subQ16=sQuery(id+"F12.wireOp",EDGE,"E74.1");var subQ18=sQuery(id+"F12.wireOp",EDGE,"E74.8");Q0=qUnion([makeQuery(id+"F12.imprint","IMPRINT",FACE,{"disambiguationData":[TD([[makeQuery(id+"F12.imprint","IMPRINT",EDGE,{"derivedFrom":subQ7}),1.0]])]}),makeQuery(id+"F12.imprint","IMPRINT",FACE,{"disambiguationData":[TD([[makeQuery(id+"F12.imprint","IMPRINT",EDGE,{"derivedFrom":subQ14}),1.0]])]}),makeQuery(id+"F12.imprint","IMPRINT",FACE,{"disambiguationData":[TD([[makeQuery(id+"F12.imprint","IMPRINT",EDGE,{"derivedFrom":subQ16}),1.0]])]}),makeQuery(id+"F12.imprint","IMPRINT",FACE,{"disambiguationData":[TD([[makeQuery(id+"F12.imprint","IMPRINT",EDGE,{"derivedFrom":subQ18}),-1.0]])]})]);}
            var Q1;
            Q1=makeQuery(id+"F5.boolean.opBoolean","SPLIT",FACE,{"disambiguationData":[TD([makeQuery(id+"F5.opExtrude","SWEPT_FACE",FACE,{"disambiguationData":[OSD([sQuery(id+"F4.wireOp",EDGE,"E41")])]})])],"derivedFrom":makeQuery(id+"F3.boolean.opBoolean","COPY",FACE,{"derivedFrom":makeQuery(id+"F3.opExtrude","CAP_FACE",FACE,{"disambiguationData":[OSD([sQuery(id+"F0.wireOp",EDGE,"E25.0"),sQuery(id+"F0.wireOp",EDGE,"E25.1"),sQuery(id+"F0.wireOp",EDGE,"E25.2"),sQuery(id+"F0.wireOp",EDGE,"E25.3"),sQuery(id+"F0.wireOp",EDGE,"E25.4"),sQuery(id+"F0.wireOp",EDGE,"E25.5"),sQuery(id+"F0.wireOp",EDGE,"E25.6"),sQuery(id+"F0.wireOp",EDGE,"E25.7")])],"isStart":false})})});
            extrude(context, id + "F13", {"entities" : qUnion([Q0]), "operationType" : NewBodyOperationType.REMOVE, "endBound" : BoundingType.UP_TO_SURFACE, "endBoundEntityFace" : qUnion([Q1]), "depth" : 25 * mm});
        }
        {
            var Q0;
            Q0=makeQuery(id+"F3.boolean.opBoolean","COPY",EDGE,{"derivedFrom":makeQuery(id+"F3.opExtrude","CAP_EDGE",EDGE,{"disambiguationData":[OSD([sQuery(id+"F0.wireOp",EDGE,"E25.6")])],"isStart":false})});
            var Q1;
            Q1=makeQuery(id+"F8.boolean.opBoolean","INTERSECT",EDGE,{"derivedFrom":[makeQuery(id+"F5.opExtrude","SWEPT_FACE",FACE,{"disambiguationData":[OSD([sQuery(id+"F4.wireOp",EDGE,"E30")])]}),makeQuery(id+"F8.opExtrude","CAP_FACE",FACE,{"disambiguationData":[OSD([sQuery(id+"F7.wireOp",EDGE,"E67")])],"isStart":false})]});
            var Q2;
            Q2=makeQuery(id+"F8.boolean.opBoolean","INTERSECT",EDGE,{"disambiguationData":[OD(1.0)],"derivedFrom":[makeQuery(id+"F5.opExtrude","SWEPT_FACE",FACE,{"disambiguationData":[OSD([sQuery(id+"F4.wireOp",EDGE,"E30")])]}),makeQuery(id+"F8.opExtrude","SWEPT_FACE",FACE,{"disambiguationData":[OSD([sQuery(id+"F7.wireOp",EDGE,"E67")])]})]});
            var Q3;
            {var subQ0=makeQuery(id+"F3.boolean.opBoolean","COPY",FACE,{"derivedFrom":makeQuery(id+"F3.opExtrude","CAP_FACE",FACE,{"disambiguationData":[OSD([sQuery(id+"F0.wireOp",EDGE,"E25.0"),sQuery(id+"F0.wireOp",EDGE,"E25.1"),sQuery(id+"F0.wireOp",EDGE,"E25.2"),sQuery(id+"F0.wireOp",EDGE,"E25.3"),sQuery(id+"F0.wireOp",EDGE,"E25.4"),sQuery(id+"F0.wireOp",EDGE,"E25.5"),sQuery(id+"F0.wireOp",EDGE,"E25.6"),sQuery(id+"F0.wireOp",EDGE,"E25.7")])],"isStart":false})});var subQ1=sQuery(id+"F4.wireOp",EDGE,"E30");Q3=makeQuery(id+"F8.boolean.opBoolean","SPLIT",EDGE,{"disambiguationData":[TD([makeQuery(id+"F5.opExtrude","SWEPT_FACE",FACE,{"disambiguationData":[OSD([sQuery(id+"F4.wireOp",EDGE,"E35.filletArc")])]})])],"derivedFrom":makeQuery(id+"F5.opExtrude","TWEAK_EDGE",EDGE,{"derivedFrom":[subQ0,makeQuery(id+"F4.imprint","IMPRINT",EDGE,{"derivedFrom":subQ1})]})});}
            var Q4;
            {var subQ0=sQuery(id+"F0.wireOp",EDGE,"E25.0");var subQ1=sQuery(id+"F0.wireOp",EDGE,"E25.1");var subQ2=sQuery(id+"F0.wireOp",EDGE,"E25.2");var subQ3=sQuery(id+"F0.wireOp",EDGE,"E25.3");var subQ4=sQuery(id+"F0.wireOp",EDGE,"E25.4");var subQ5=sQuery(id+"F0.wireOp",EDGE,"E25.5");var subQ6=sQuery(id+"F0.wireOp",EDGE,"E25.6");var subQ7=sQuery(id+"F0.wireOp",EDGE,"E25.7");Q4=makeQuery(id+"F8.boolean.opBoolean","INTERSECT",EDGE,{"derivedFrom":[makeQuery(id+"F5.boolean.opBoolean","SPLIT",FACE,{"disambiguationData":[TD([makeQuery(id+"F2.opExtrude","SWEPT_FACE",FACE,{"disambiguationData":[OSD([subQ0])]})])],"derivedFrom":makeQuery(id+"F3.boolean.opBoolean","COPY",FACE,{"derivedFrom":makeQuery(id+"F3.opExtrude","CAP_FACE",FACE,{"disambiguationData":[OSD([subQ0,subQ1,subQ2,subQ3,subQ4,subQ5,subQ6,subQ7])],"isStart":false})})}),makeQuery(id+"F8.opExtrude","SWEPT_FACE",FACE,{"disambiguationData":[OSD([sQuery(id+"F7.wireOp",EDGE,"E67")])]})]});}
            var Q5;
            Q5=makeQuery(id+"F8.boolean.opBoolean","INTERSECT",EDGE,{"disambiguationData":[OD(0.0)],"derivedFrom":[makeQuery(id+"F5.opExtrude","SWEPT_FACE",FACE,{"disambiguationData":[OSD([sQuery(id+"F4.wireOp",EDGE,"E30")])]}),makeQuery(id+"F8.opExtrude","SWEPT_FACE",FACE,{"disambiguationData":[OSD([sQuery(id+"F7.wireOp",EDGE,"E67")])]})]});
            fillet(context, id + "F14", {"entities" : qUnion([Q0, Q1, Q2, Q3, Q4, Q5]), "radius" : 3 * mm, "tangentPropagation" : true, "allowEdgeOverflow" : false});
        }
        {
            var Q0;
            Q0=makeQuery(id+"F1.opExtrude","CAP_EDGE",EDGE,{"disambiguationData":[OSD([sQuery(id+"F0.wireOp",EDGE,"E1.bottom")])],"isStart":false});
            fillet(context, id + "F15", {"entities" : qUnion([Q0]), "radius" : 2 * mm, "tangentPropagation" : true, "allowEdgeOverflow" : false});
        }
        {
            var Q0;
            {var subQ0=sQuery(id+"F0.wireOp",EDGE,"E22.filletArc");var subQ1=sQuery(id+"F0.wireOp",EDGE,"E7");var subQ2=sQuery(id+"F0.wireOp",EDGE,"E6");var subQ3=sQuery(id+"F0.wireOp",EDGE,"E5");var subQ4=sQuery(id+"F0.wireOp",EDGE,"E4");var subQ5=sQuery(id+"F0.wireOp",EDGE,"E1.bottom");var subQ6=sQuery(id+"F0.wireOp",EDGE,"E21.filletArc");var subQ7=sQuery(id+"F0.wireOp",EDGE,"E1.top");var subQ8=sQuery(id+"F0.wireOp",EDGE,"E1.left");var subQ9=sQuery(id+"F0.wireOp",EDGE,"E1.right");var subQ10=sQuery(id+"F0.wireOp",EDGE,"E23.filletArc");var subQ11=sQuery(id+"F0.wireOp",EDGE,"E24.filletArc");Q0=makeQuery(id+"F2.boolean.opBoolean","SPLIT",FACE,{"disambiguationData":[TD([makeQuery(id+"F1.opExtrude","SWEPT_FACE",FACE,{"disambiguationData":[OSD([subQ5])]})])],"derivedFrom":makeQuery(id+"F1.opExtrude","CAP_FACE",FACE,{"disambiguationData":[OSD([subQ5,subQ7,subQ8,subQ9,subQ4,subQ3,subQ2,subQ1,subQ6,subQ0,subQ10,subQ11])],"isStart":true})});}
            var sketch = newSketch(context, id + "F16", { "sketchPlane" : qUnion([Q0])});
            skLineSegment(sketch, "E79.0", {"start": v(-80, 80) * mm, "end": v(80, 80) * mm});
            skArc(sketch, "E79.1", {"start": v(-80, 80) * mm, "mid": v(-87.07, 77.07) * mm, "end": v(-90, 70) * mm});
            skLineSegment(sketch, "E79.2", {"start": v(-90, -70) * mm, "end": v(-90, 70) * mm});
            skArc(sketch, "E79.3", {"start": v(-90, -70) * mm, "mid": v(-87.07, -77.07) * mm, "end": v(-80, -80) * mm});
            skLineSegment(sketch, "E79.4", {"start": v(-80, -80) * mm, "end": v(80, -80) * mm});
            skArc(sketch, "E79.5", {"start": v(80, -80) * mm, "mid": v(87.07, -77.07) * mm, "end": v(90, -70) * mm});
            skLineSegment(sketch, "E79.6", {"start": v(90, -70) * mm, "end": v(90, 70) * mm});
            skArc(sketch, "E79.7", {"start": v(90, 70) * mm, "mid": v(87.07, 77.07) * mm, "end": v(80, 80) * mm});
            skCircle(sketch, "E79.8", {"center": v(-60, 53.33) * mm, "radius": 4 * mm});
            skCircle(sketch, "E79.9", {"center": v(-60, -53.33) * mm, "radius": 4 * mm});
            skCircle(sketch, "E79.10", {"center": v(60, -53.33) * mm, "radius": 4 * mm});
            skCircle(sketch, "E79.11", {"center": v(60, 53.33) * mm, "radius": 4 * mm});
            skArc(sketch, "E79.12", {"start": v(52.38, 47.01) * mm, "mid": v(0, 53.33) * mm, "end": v(-52.38, 47.01) * mm});
            skArc(sketch, "E79.13", {"start": v(-52.38, 47.01) * mm, "mid": v(-57.87, 43.47) * mm, "end": v(-60, 37.3) * mm});
            skLineSegment(sketch, "E79.14", {"start": v(-60, 37.3) * mm, "end": v(-60, -37.3) * mm});
            skArc(sketch, "E79.15", {"start": v(-60, -37.3) * mm, "mid": v(-57.87, -43.47) * mm, "end": v(-52.38, -47.01) * mm});
            skArc(sketch, "E79.16", {"start": v(-52.38, -47.01) * mm, "mid": v(0, -53.33) * mm, "end": v(52.38, -47.01) * mm});
            skArc(sketch, "E79.17", {"start": v(52.38, -47.01) * mm, "mid": v(57.87, -43.47) * mm, "end": v(60, -37.3) * mm});
            skLineSegment(sketch, "E79.18", {"start": v(60, 37.3) * mm, "end": v(60, -37.3) * mm});
            skArc(sketch, "E79.19", {"start": v(60, 37.3) * mm, "mid": v(57.87, 43.47) * mm, "end": v(52.38, 47.01) * mm});
            skLineSegment(sketch, "E80", {"start": v(0, 80) * mm, "end": v(0, 110) * mm, "construction": true});
            skLineSegment(sketch, "E81", {"start": v(-32.76, 80) * mm, "end": v(-14.76, 98) * mm});
            skLineSegment(sketch, "E82", {"start": v(-14.76, 98) * mm, "end": v(-14.76, 110) * mm});
            skLineSegment(sketch, "E83", {"start": v(33.24, 80) * mm, "end": v(15.24, 98) * mm});
            skLineSegment(sketch, "E84", {"start": v(15.24, 98) * mm, "end": v(15.24, 110) * mm});
            skCircle(sketch, "E85", {"center": v(0, 110) * mm, "radius": 6 * mm});
            skArc(sketch, "E86", {"start": v(15.24, 110) * mm, "mid": v(0.24, 125) * mm, "end": v(-14.76, 110) * mm});
            skLineSegment(sketch, "E87", {"start": v(-90, 0) * mm, "end": v(90, 0) * mm, "construction": true});
            skArc(sketch, "E88.MirrorCS", {"start": v(15.24, -110) * mm, "mid": v(0.24, -125) * mm, "end": v(-14.76, -110) * mm});
            skLineSegment(sketch, "E89.MirrorCS", {"start": v(15.24, -98) * mm, "end": v(15.24, -110) * mm});
            skLineSegment(sketch, "E90.MirrorCS", {"start": v(-14.76, -98) * mm, "end": v(-14.76, -110) * mm});
            skLineSegment(sketch, "E91.MirrorCS", {"start": v(-32.76, -80) * mm, "end": v(-14.76, -98) * mm});
            skLineSegment(sketch, "E92.MirrorCS", {"start": v(33.24, -80) * mm, "end": v(15.24, -98) * mm});
            skLineSegment(sketch, "E93.MirrorCS", {"start": v(0, -80) * mm, "end": v(0, -110) * mm, "construction": true});
            skCircle(sketch, "E94.MirrorC", {"center": v(0, -110) * mm, "radius": 6 * mm});
            skSolve(sketch);
        }
        {
            var Q0;
            {var subQ1=sQuery(id+"F16.wireOp",EDGE,"E79.1");Q0=makeQuery(id+"F16.imprint","IMPRINT",FACE,{"disambiguationData":[TD([[makeQuery(id+"F16.imprint","IMPRINT",EDGE,{"derivedFrom":subQ1}),1.0]])]});}
            var Q1;
            {var subQ1=sQuery(id+"F16.wireOp",EDGE,"E81");Q1=makeQuery(id+"F16.imprint","IMPRINT",FACE,{"disambiguationData":[TD([[makeQuery(id+"F16.imprint","IMPRINT",EDGE,{"derivedFrom":subQ1}),-1.0]])]});}
            var Q2;
            Q2=makeQuery(id+"F16.imprint","IMPRINT",FACE,{"disambiguationData":[TD([[makeQuery(id+"F16.imprint","IMPRINT",EDGE,{"derivedFrom":sQuery(id+"F16.wireOp",EDGE,"E89.MirrorCS")}),-1.0]])]});
            extrude(context, id + "F17", {"entities" : qUnion([Q0, Q1, Q2]), "operationType" : NewBodyOperationType.ADD, "endBound" : BoundingType.SYMMETRIC, "depth" : 6 * mm});
        }
    });
